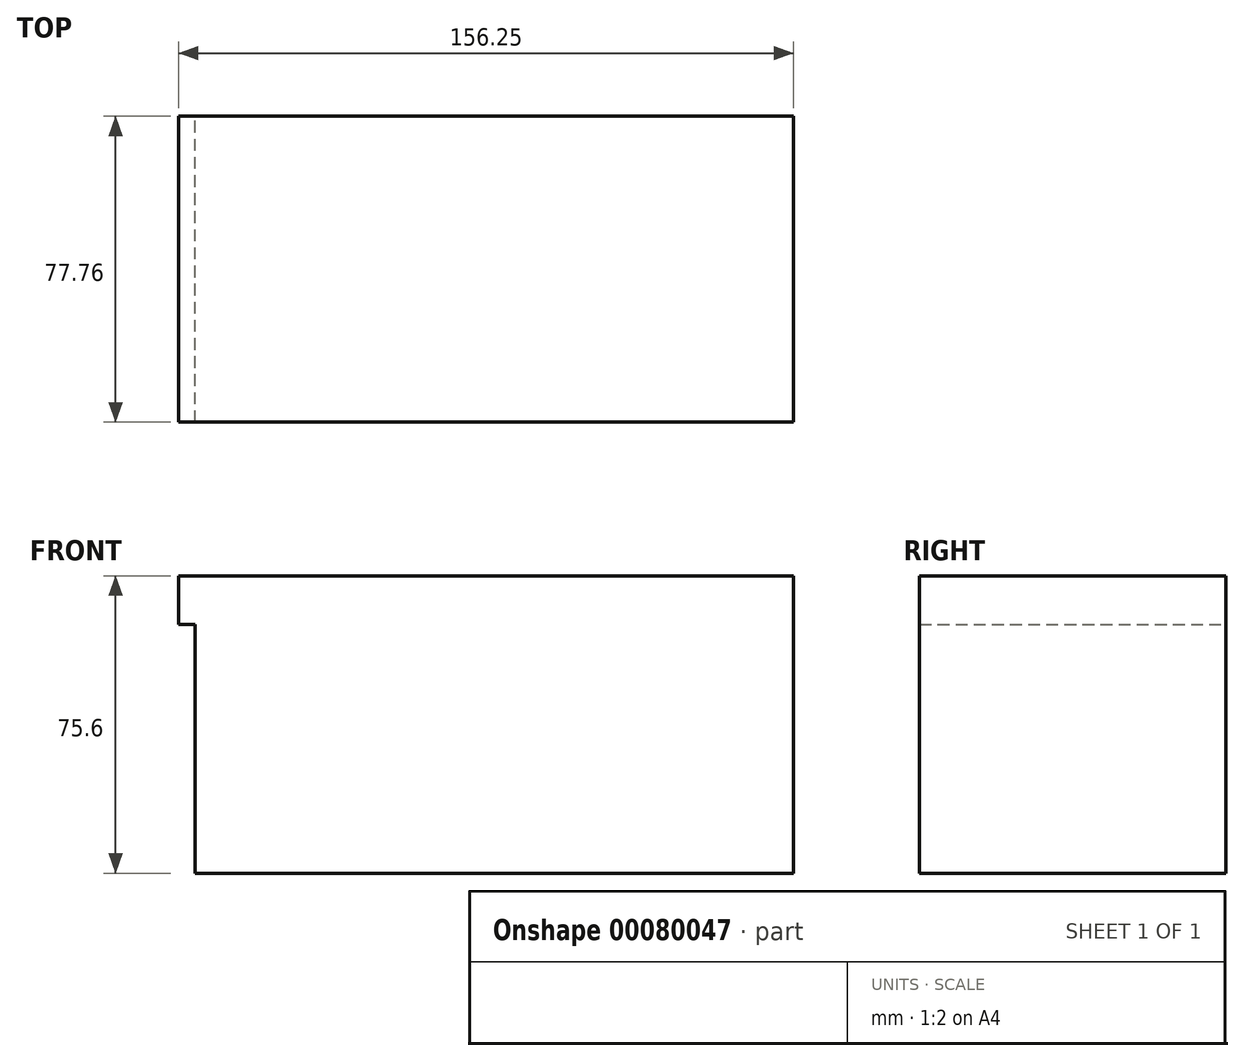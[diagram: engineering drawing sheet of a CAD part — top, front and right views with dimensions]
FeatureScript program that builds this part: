
annotation { "Feature Type Name" : "Feature", "Feature Type Description" : "" }
export const myFeature = defineFeature(function(context is Context, id is Id, definition is map)
    precondition{}
    {
        {
            var Q0;
            Q0=qCreatedBy(makeId("Front.planeOp"),FACE);
            var sketch = newSketch(context, id + "F0", { "sketchPlane" : qUnion([Q0])});
            skLineSegment(sketch, "E0.bottom", {"start": v(-75.43, 75.6) * mm, "end": v(76.65, 75.6) * mm});
            skLineSegment(sketch, "E0.top", {"start": v(-75.43, 0) * mm, "end": v(76.65, 0) * mm});
            skLineSegment(sketch, "E0.left", {"start": v(-75.43, 75.6) * mm, "end": v(-75.43, 0) * mm});
            skLineSegment(sketch, "E0.right", {"start": v(76.65, 75.6) * mm, "end": v(76.65, 0) * mm});
            skLineSegment(sketch, "E1.bottom", {"start": v(-75.43, 75.6) * mm, "end": v(-79.6, 75.6) * mm});
            skLineSegment(sketch, "E1.top", {"start": v(-75.43, 63.27) * mm, "end": v(-79.6, 63.27) * mm});
            skLineSegment(sketch, "E1.left", {"start": v(-75.43, 75.6) * mm, "end": v(-75.43, 63.27) * mm});
            skLineSegment(sketch, "E1.right", {"start": v(-79.6, 75.6) * mm, "end": v(-79.6, 63.27) * mm});
            skSolve(sketch);
        }
        {
            var Q0;
            Q0=makeQuery(id+"F0.imprint","IMPRINT",FACE,{"disambiguationData":[TD([[makeQuery(id+"F0.imprint","IMPRINT",EDGE,{"derivedFrom":sQuery(id+"F0.wireOp",EDGE,"E0.bottom")}),-1.0]])]});
            var Q1;
            Q1=makeQuery(id+"F0.imprint","IMPRINT",FACE,{"disambiguationData":[TD([[makeQuery(id+"F0.imprint","IMPRINT",EDGE,{"derivedFrom":sQuery(id+"F0.wireOp",EDGE,"E1.bottom")}),1.0]])]});
            extrude(context, id + "F1", {"entities" : qUnion([Q0, Q1]), "depth" : 77.76 * mm});
        }
    });
